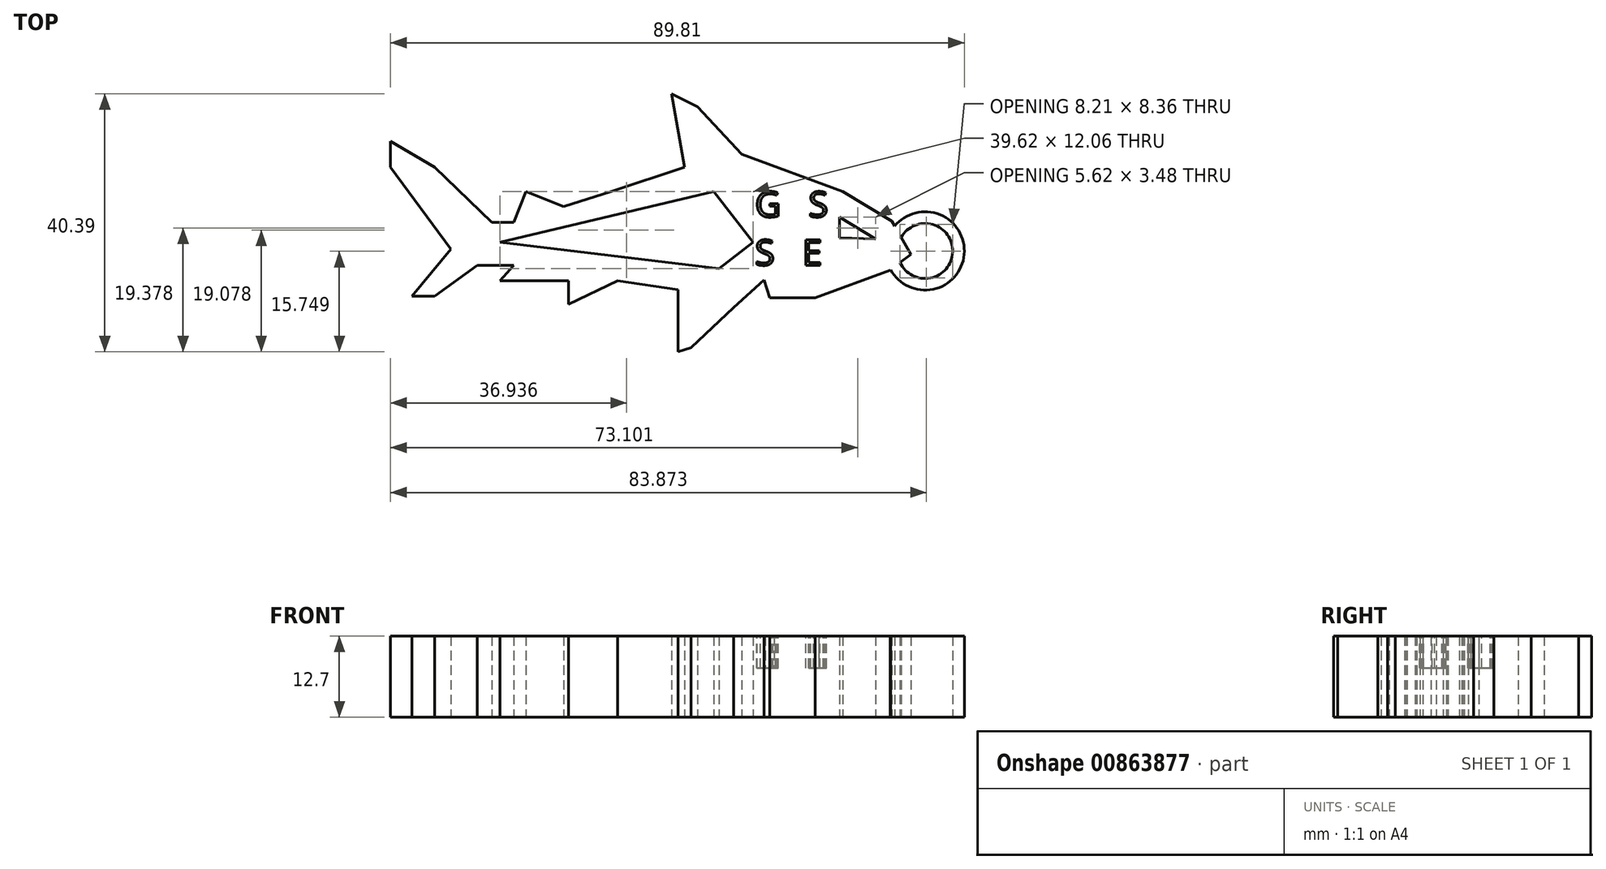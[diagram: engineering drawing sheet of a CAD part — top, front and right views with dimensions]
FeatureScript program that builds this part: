
annotation { "Feature Type Name" : "Feature", "Feature Type Description" : "" }
export const myFeature = defineFeature(function(context is Context, id is Id, definition is map)
    precondition{}
    {
        {
            var Q0;
            Q0=qCreatedBy(makeId("Top.planeOp"),FACE);
            var sketch = newSketch(context, id + "F0", { "sketchPlane" : qUnion([Q0])});
            skLineSegment(sketch, "E0", {"start": v(22.57, 5.82) * mm, "end": v(38.42, 0) * mm});
            skLineSegment(sketch, "E1", {"start": v(22.57, 5.82) * mm, "end": v(15.67, 13.23) * mm});
            skLineSegment(sketch, "E2", {"start": v(15.67, 13.23) * mm, "end": v(11.58, 15.28) * mm});
            skLineSegment(sketch, "E3", {"start": v(11.58, 15.28) * mm, "end": v(13.63, 3.78) * mm});
            skLineSegment(sketch, "E4", {"start": v(13.63, 3.78) * mm, "end": v(2.13, 0) * mm});
            skLineSegment(sketch, "E5", {"start": v(2.13, 0) * mm, "end": v(-5.28, -2.36) * mm});
            skLineSegment(sketch, "E6", {"start": v(-5.28, -2.36) * mm, "end": v(-11.16, 0) * mm});
            skLineSegment(sketch, "E7", {"start": v(-11.16, 0) * mm, "end": v(-13.1, -4.85) * mm});
            skLineSegment(sketch, "E8", {"start": v(-13.1, -4.85) * mm, "end": v(-16.53, -4.85) * mm});
            skLineSegment(sketch, "E9", {"start": v(-16.53, -4.85) * mm, "end": v(-25.48, 3.78) * mm});
            skLineSegment(sketch, "E10", {"start": v(-25.48, 3.78) * mm, "end": v(-32.38, 7.86) * mm});
            skLineSegment(sketch, "E11", {"start": v(-32.38, 7.86) * mm, "end": v(-32.38, 3.78) * mm});
            skLineSegment(sketch, "E12", {"start": v(-32.38, 3.78) * mm, "end": v(-22.92, -9) * mm});
            skLineSegment(sketch, "E13", {"start": v(-22.92, -9) * mm, "end": v(-29.05, -16.42) * mm});
            skLineSegment(sketch, "E14", {"start": v(-29.05, -16.42) * mm, "end": v(-25.48, -16.42) * mm});
            skLineSegment(sketch, "E15", {"start": v(-25.48, -16.42) * mm, "end": v(-18.83, -11.56) * mm});
            skLineSegment(sketch, "E16", {"start": v(-18.83, -11.56) * mm, "end": v(-13.1, -11.56) * mm});
            skLineSegment(sketch, "E17", {"start": v(-13.1, -11.56) * mm, "end": v(-15.25, -13.99) * mm});
            skPoint(sketch, "E17.endSnap0", {"position": v(-22.15, -13.99) * mm});
            skLineSegment(sketch, "E18", {"start": v(-15.25, -13.99) * mm, "end": v(-9.88, -13.99) * mm});
            skLineSegment(sketch, "E19", {"start": v(-9.88, -13.99) * mm, "end": v(-4.52, -13.99) * mm});
            skLineSegment(sketch, "E20", {"start": v(-4.52, -13.99) * mm, "end": v(-4.52, -17.7) * mm});
            skLineSegment(sketch, "E21", {"start": v(-4.52, -17.7) * mm, "end": v(3.15, -13.99) * mm});
            skPoint(sketch, "E22", {"position": v(12.6, -15.4) * mm});
            skPoint(sketch, "E23", {"position": v(12.6, -25.1) * mm});
            skLineSegment(sketch, "E24", {"start": v(3.15, -13.99) * mm, "end": v(12.6, -15.4) * mm});
            skLineSegment(sketch, "E25", {"start": v(12.6, -25.1) * mm, "end": v(12.6, -15.4) * mm});
            skLineSegment(sketch, "E26", {"start": v(12.6, -25.1) * mm, "end": v(14.63, -24.46) * mm});
            skLineSegment(sketch, "E27", {"start": v(14.63, -24.46) * mm, "end": v(21.3, -18.2) * mm});
            skLineSegment(sketch, "E28", {"start": v(21.3, -18.2) * mm, "end": v(26.06, -13.86) * mm});
            skLineSegment(sketch, "E29", {"start": v(26.06, -13.86) * mm, "end": v(26.96, -16.67) * mm});
            skLineSegment(sketch, "E30", {"start": v(26.96, -16.67) * mm, "end": v(34.08, -16.67) * mm});
            skLineSegment(sketch, "E31", {"start": v(18.23, 0) * mm, "end": v(24.36, -7.98) * mm});
            skLineSegment(sketch, "E32", {"start": v(24.36, -7.98) * mm, "end": v(19.05, -12.06) * mm});
            skLineSegment(sketch, "E33", {"start": v(19.05, -12.06) * mm, "end": v(-15.25, -7.98) * mm});
            skLineSegment(sketch, "E34", {"start": v(-15.25, -7.98) * mm, "end": v(18.23, 0) * mm});
            skLineSegment(sketch, "E35", {"start": v(38.42, 0) * mm, "end": v(46.09, -4.66) * mm});
            skLineSegment(sketch, "E36", {"start": v(34.08, -16.67) * mm, "end": v(45.83, -12.33) * mm});
            skLineSegment(sketch, "E37", {"start": v(45.83, -12.33) * mm, "end": v(49.08, -9.83) * mm});
            skLineSegment(sketch, "E38", {"start": v(49.08, -9.83) * mm, "end": v(46.09, -4.66) * mm});
            skPoint(sketch, "E39", {"position": v(37.91, -4) * mm});
            skPoint(sketch, "E39.positionSnap0", {"position": v(21.3, -4) * mm});
            skPoint(sketch, "E40", {"position": v(37.91, -7.25) * mm});
            skPoint(sketch, "E40.positionSnap0", {"position": v(47.59, -7.25) * mm});
            skPoint(sketch, "E41", {"position": v(43.53, -7.47) * mm});
            skLineSegment(sketch, "E42", {"start": v(37.91, -4) * mm, "end": v(37.91, -7.25) * mm});
            skLineSegment(sketch, "E43", {"start": v(37.91, -7.25) * mm, "end": v(43.53, -7.47) * mm});
            skLineSegment(sketch, "E44", {"start": v(43.53, -7.47) * mm, "end": v(37.91, -4) * mm});
            skSolve(sketch);
        }
        {
            var Q0;
            Q0=makeQuery(id+"F0.imprint","IMPRINT",FACE,{"disambiguationData":[TD([[makeQuery(id+"F0.imprint","IMPRINT",EDGE,{"derivedFrom":sQuery(id+"F0.wireOp",EDGE,"E0")}),-1.0]])]});
            extrude(context, id + "F1", {"entities" : qUnion([Q0]), "depth" : 12.7 * mm, "offsetDistance" : 25.4 * mm});
        }
        {
            var Q0;
            Q0=qCreatedBy(makeId("Top.planeOp"),FACE);
            var sketch = newSketch(context, id + "F2", { "sketchPlane" : qUnion([Q0])});
            skCircle(sketch, "E45", {"center": v(51.3, -9.32) * mm, "radius": 6.14 * mm});
            skCircle(sketch, "E46", {"center": v(51.3, -9.32) * mm, "radius": 4.3 * mm});
            skSolve(sketch);
        }
        {
            var Q0;
            Q0 = qSketchRegion(id + "F2", true);
            extrude(context, id + "F3", {"entities" : qUnion([Q0]), "operationType" : NewBodyOperationType.ADD, "depth" : 12.7 * mm, "offsetDistance" : 25.4 * mm});
        }
        {
            var Q0;
            Q0=makeQuery(id+"F3.boolean.opBoolean","MERGE",FACE,{"derivedFrom":[makeQuery(id+"F1.opExtrude","CAP_FACE",FACE,{"disambiguationData":[OSD([sQuery(id+"F0.wireOp",EDGE,"E0"),sQuery(id+"F0.wireOp",EDGE,"E1"),sQuery(id+"F0.wireOp",EDGE,"E2"),sQuery(id+"F0.wireOp",EDGE,"E3"),sQuery(id+"F0.wireOp",EDGE,"E4"),sQuery(id+"F0.wireOp",EDGE,"E5"),sQuery(id+"F0.wireOp",EDGE,"E6"),sQuery(id+"F0.wireOp",EDGE,"E7"),sQuery(id+"F0.wireOp",EDGE,"E8"),sQuery(id+"F0.wireOp",EDGE,"E9"),sQuery(id+"F0.wireOp",EDGE,"E10"),sQuery(id+"F0.wireOp",EDGE,"E11"),sQuery(id+"F0.wireOp",EDGE,"E12"),sQuery(id+"F0.wireOp",EDGE,"E13"),sQuery(id+"F0.wireOp",EDGE,"E14"),sQuery(id+"F0.wireOp",EDGE,"E15"),sQuery(id+"F0.wireOp",EDGE,"E16"),sQuery(id+"F0.wireOp",EDGE,"E17"),sQuery(id+"F0.wireOp",EDGE,"E18"),sQuery(id+"F0.wireOp",EDGE,"E19"),sQuery(id+"F0.wireOp",EDGE,"E20"),sQuery(id+"F0.wireOp",EDGE,"E21"),sQuery(id+"F0.wireOp",EDGE,"E24"),sQuery(id+"F0.wireOp",EDGE,"E25"),sQuery(id+"F0.wireOp",EDGE,"E26"),sQuery(id+"F0.wireOp",EDGE,"E27"),sQuery(id+"F0.wireOp",EDGE,"E28"),sQuery(id+"F0.wireOp",EDGE,"E29"),sQuery(id+"F0.wireOp",EDGE,"E30"),sQuery(id+"F0.wireOp",EDGE,"E31"),sQuery(id+"F0.wireOp",EDGE,"E32"),sQuery(id+"F0.wireOp",EDGE,"E33"),sQuery(id+"F0.wireOp",EDGE,"E34"),sQuery(id+"F0.wireOp",EDGE,"E35"),sQuery(id+"F0.wireOp",EDGE,"E36"),sQuery(id+"F0.wireOp",EDGE,"E37"),sQuery(id+"F0.wireOp",EDGE,"E38"),sQuery(id+"F0.wireOp",EDGE,"E42"),sQuery(id+"F0.wireOp",EDGE,"E43"),sQuery(id+"F0.wireOp",EDGE,"E44")])],"isStart":false}),makeQuery(id+"F3.opExtrude","CAP_FACE",FACE,{"disambiguationData":[OSD([sQuery(id+"F2.wireOp",EDGE,"E45"),sQuery(id+"F2.wireOp",EDGE,"E46")])],"isStart":false})]});
            var sketch = newSketch(context, id + "F4", { "sketchPlane" : qUnion([Q0])});
            skText(sketch, "E47", { "text": "G   S\nS   E", "fontName": "OpenSans-Regular.ttf"});
            const initialGuessF4  = {"E47": [0.02468, -0.004, 1, 0, 0.004]};
            skSetInitialGuess(sketch, initialGuessF4);
            skSolve(sketch);
        }
        {
            var Q0;
            Q0 = qSketchRegion(id + "F4", true);
            extrude(context, id + "F5", {"entities" : qUnion([Q0]), "operationType" : NewBodyOperationType.REMOVE, "oppositeDirection" : true, "depth" : 5 * mm, "offsetDistance" : 25 * mm});
        }
    });
